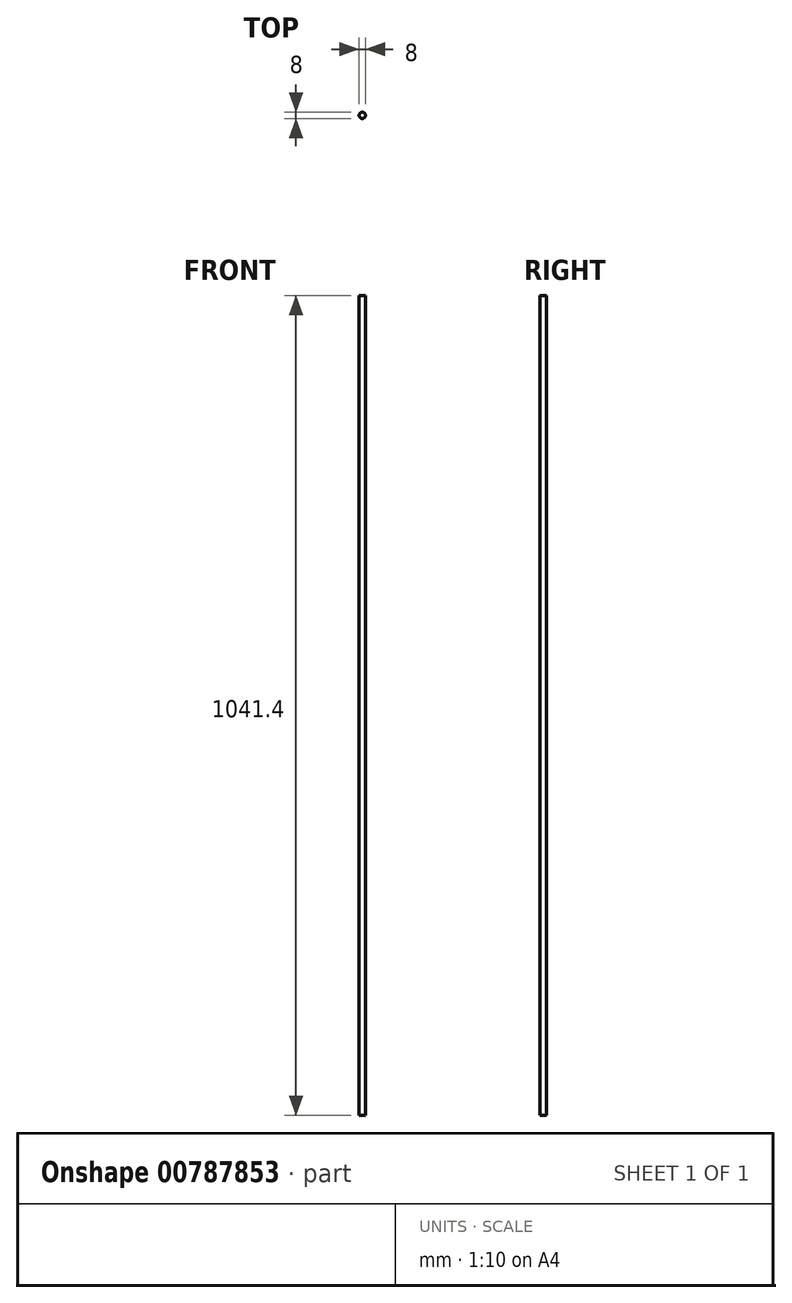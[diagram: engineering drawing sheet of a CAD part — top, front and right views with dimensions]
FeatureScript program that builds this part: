
annotation { "Feature Type Name" : "Feature", "Feature Type Description" : "" }
export const myFeature = defineFeature(function(context is Context, id is Id, definition is map)
    precondition{}
    {
        {
            var Q0;
            Q0=qCreatedBy(makeId("Top.planeOp"),FACE);
            var sketch = newSketch(context, id + "F0", { "sketchPlane" : qUnion([Q0])});
            skCircle(sketch, "E0", {"center": v(0, 0) * mm, "radius": 4 * mm});
            skSolve(sketch);
        }
        {
            var Q0;
            Q0 = qSketchRegion(id + "F0", true);
            extrude(context, id + "F1", {"entities" : qUnion([Q0]), "depth" : 1041.4 * mm, "offsetDistance" : 25.4 * mm});
        }
    });
